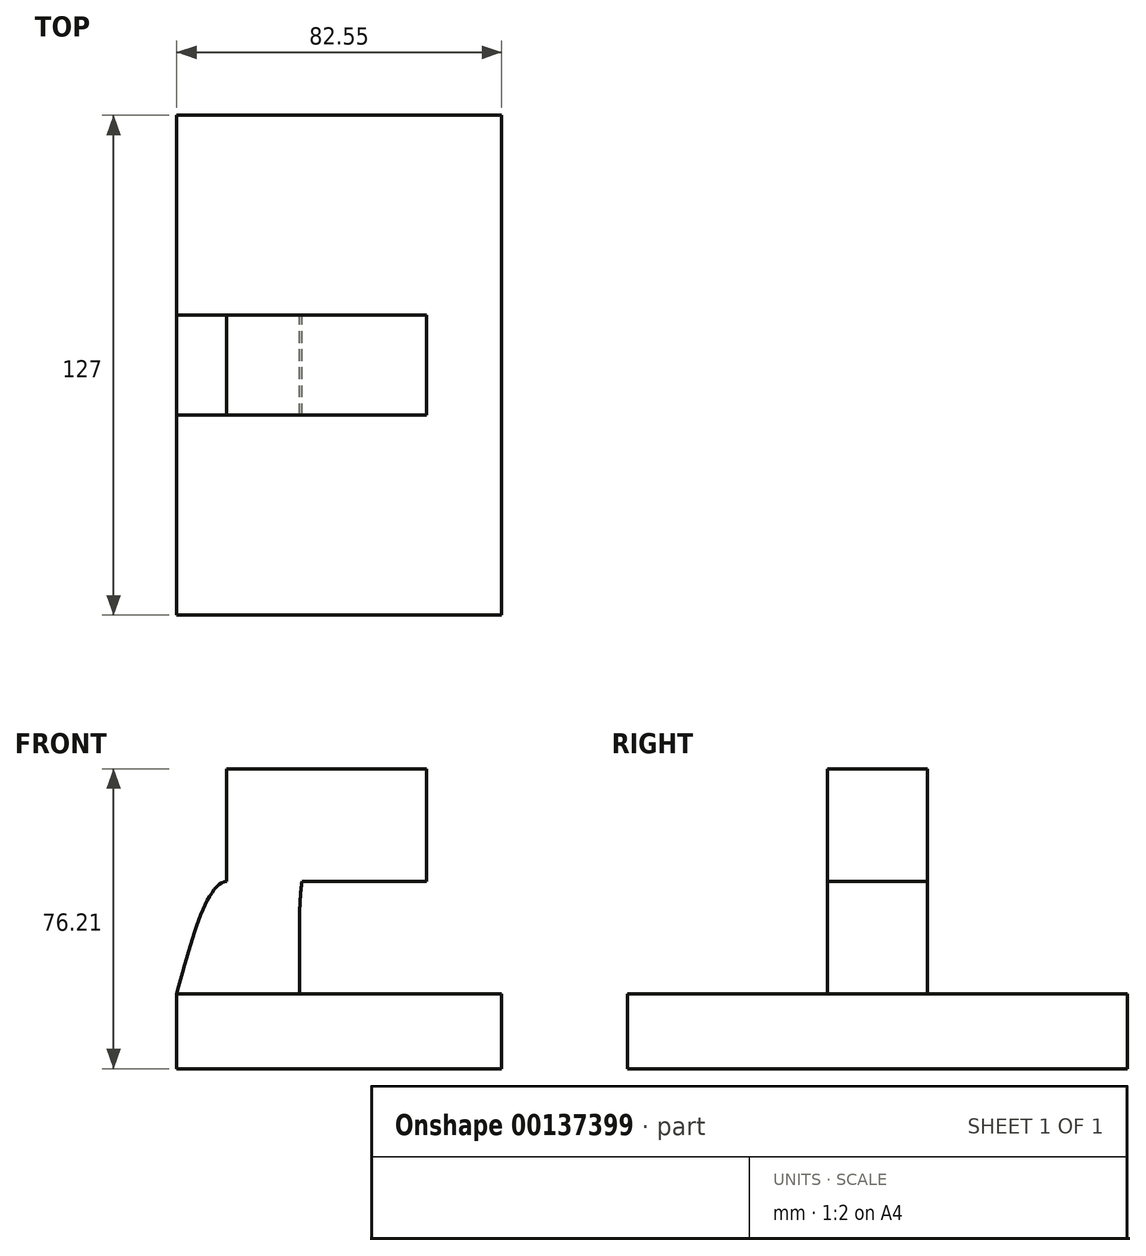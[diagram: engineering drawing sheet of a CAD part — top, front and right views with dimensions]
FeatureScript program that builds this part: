
annotation { "Feature Type Name" : "Feature", "Feature Type Description" : "" }
export const myFeature = defineFeature(function(context is Context, id is Id, definition is map)
    precondition{}
    {
        {
            var Q0;
            Q0=qCreatedBy(makeId("Front.planeOp"),FACE);
            var sketch = newSketch(context, id + "F0", { "sketchPlane" : qUnion([Q0])});
            skLineSegment(sketch, "E0.bottom", {"start": v(41.28, -9.52) * mm, "end": v(-41.28, -9.53) * mm});
            skLineSegment(sketch, "E0.top", {"start": v(41.28, 9.53) * mm, "end": v(-41.28, 9.53) * mm});
            skLineSegment(sketch, "E0.left", {"start": v(41.28, -9.52) * mm, "end": v(41.28, 9.53) * mm});
            skLineSegment(sketch, "E0.right", {"start": v(-41.28, -9.53) * mm, "end": v(-41.28, 9.53) * mm});
            skPoint(sketch, "E0.middle", {"position": v(0, 0) * mm});
            skLineSegment(sketch, "E1.bottom", {"start": v(-28.58, 66.68) * mm, "end": v(22.23, 66.68) * mm});
            skLineSegment(sketch, "E1.top", {"start": v(-28.58, 38.1) * mm, "end": v(22.23, 38.1) * mm});
            skLineSegment(sketch, "E1.left", {"start": v(-28.58, 66.68) * mm, "end": v(-28.58, 38.1) * mm});
            skLineSegment(sketch, "E1.right", {"start": v(22.23, 66.68) * mm, "end": v(22.23, 38.1) * mm});
            skPoint(sketch, "E1.middle", {"position": v(-3.18, 52.39) * mm});
            skLineSegment(sketch, "E2", {"start": v(41.28, 9.53) * mm, "end": v(41.28, 29) * mm});
            skArc(sketch, "E3", {"start": v(41.27, 29) * mm, "mid": v(44.47, 38.55) * mm, "end": v(52.77, 44.26) * mm});
            skLineSegment(sketch, "E4", {"start": v(52.77, 44.26) * mm, "end": v(66.11, 44.26) * mm});
            skLineSegment(sketch, "E5.0", {"start": v(48.07, 95.58) * mm, "end": v(66.11, 95.58) * mm});
            skArc(sketch, "E5.1", {"start": v(-10.05, 29) * mm, "mid": v(6.52, 73.19) * mm, "end": v(48.07, 95.58) * mm});
            skLineSegment(sketch, "E5.2", {"start": v(-10.05, 9.53) * mm, "end": v(-10.05, 29) * mm});
            skFitSpline(sketch, "E6", {"points": [v(-41.28, 9.53) * mm, v(-28.58, 38.1) * mm, v(-10.05, 11.87) * mm], "startDerivative": vector(22.78, 84.76) * mm, "endDerivative": vector(39.63, -79.72) * mm});
            skSolve(sketch);
        }
        {
            var Q0;
            Q0=makeQuery(id+"F0.imprint","IMPRINT",FACE,{"disambiguationData":[TD([[makeQuery(id+"F0.imprint","IMPRINT",EDGE,{"derivedFrom":sQuery(id+"F0.wireOp",EDGE,"E0.bottom")}),-1.0]])]});
            extrude(context, id + "F1", {"entities" : qUnion([Q0]), "endBound" : BoundingType.SYMMETRIC, "depth" : 127 * mm});
        }
        {
            var Q0;
            Q0 = qSketchRegion(id + "F0", true);
            extrude(context, id + "F2", {"entities" : qUnion([Q0]), "operationType" : NewBodyOperationType.ADD, "endBound" : BoundingType.SYMMETRIC, "depth" : 25.4 * mm});
        }
    });
